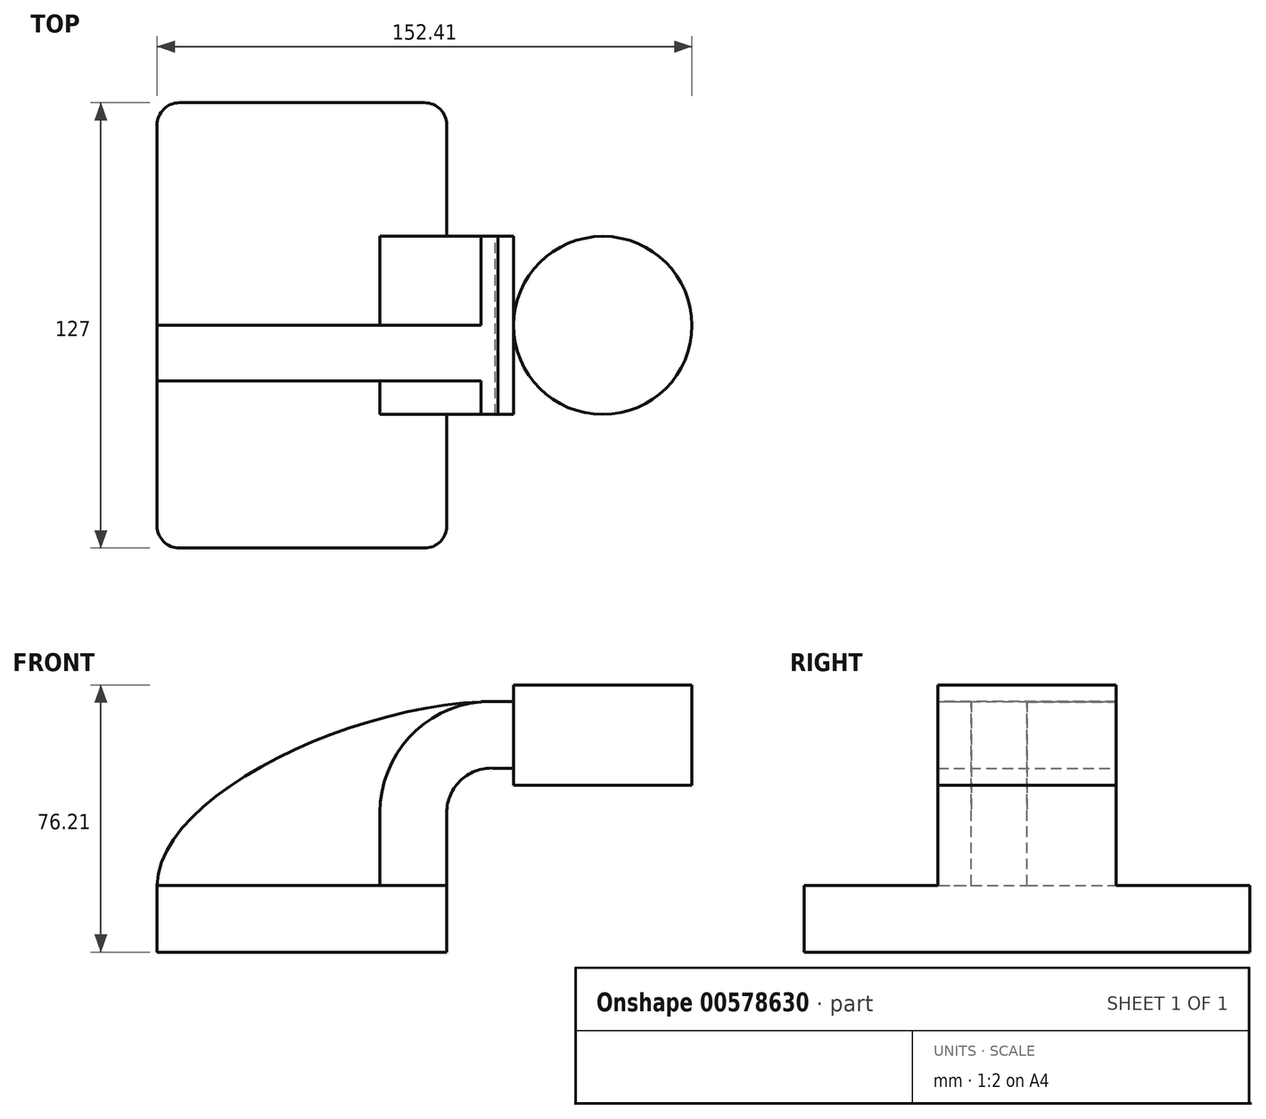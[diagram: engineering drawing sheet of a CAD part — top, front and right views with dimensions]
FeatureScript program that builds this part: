
annotation { "Feature Type Name" : "Feature", "Feature Type Description" : "" }
export const myFeature = defineFeature(function(context is Context, id is Id, definition is map)
    precondition{}
    {
        {
            var Q0;
            Q0=qCreatedBy(makeId("Front.planeOp"),FACE);
            var sketch = newSketch(context, id + "F0", { "sketchPlane" : qUnion([Q0])});
            skLineSegment(sketch, "E0.bottom", {"start": v(-41.28, 9.52) * mm, "end": v(41.27, 9.53) * mm});
            skLineSegment(sketch, "E0.top", {"start": v(-41.28, -9.53) * mm, "end": v(41.28, -9.53) * mm});
            skLineSegment(sketch, "E0.left", {"start": v(-41.28, 9.52) * mm, "end": v(-41.27, -9.53) * mm});
            skLineSegment(sketch, "E0.right", {"start": v(41.28, 9.53) * mm, "end": v(41.28, -9.52) * mm});
            skPoint(sketch, "E0.middle", {"position": v(0, 0) * mm});
            skLineSegment(sketch, "E1.bottom", {"start": v(60.32, 66.68) * mm, "end": v(111.12, 66.68) * mm});
            skLineSegment(sketch, "E1.top", {"start": v(60.33, 38.1) * mm, "end": v(111.13, 38.1) * mm});
            skLineSegment(sketch, "E1.left", {"start": v(60.32, 66.67) * mm, "end": v(60.33, 38.1) * mm});
            skLineSegment(sketch, "E1.right", {"start": v(111.12, 66.67) * mm, "end": v(111.13, 38.1) * mm});
            skPoint(sketch, "E1.middle", {"position": v(85.73, 52.39) * mm});
            skLineSegment(sketch, "E2", {"start": v(41.27, 9.53) * mm, "end": v(41.27, 30.28) * mm});
            skArc(sketch, "E3", {"start": v(41.28, 30.28) * mm, "mid": v(45.42, 39.64) * mm, "end": v(55.15, 42.88) * mm});
            skLineSegment(sketch, "E4", {"start": v(55.15, 42.88) * mm, "end": v(85.73, 42.88) * mm});
            skLineSegment(sketch, "E5", {"start": v(85.73, 42.88) * mm, "end": v(82.92, 42.88) * mm});
            skLineSegment(sketch, "E6.0", {"start": v(55.85, 61.93) * mm, "end": v(85.72, 61.93) * mm});
            skArc(sketch, "E6.1", {"start": v(22.23, 30.28) * mm, "mid": v(32.2, 53.37) * mm, "end": v(55.85, 61.93) * mm});
            skLineSegment(sketch, "E6.2", {"start": v(22.22, 9.53) * mm, "end": v(22.22, 30.28) * mm});
            skLineSegment(sketch, "E7", {"start": v(85.73, 38.1) * mm, "end": v(85.73, 66.67) * mm});
            skFitSpline(sketch, "E8", {"points": [v(-41.28, 9.53) * mm, v(55.85, 61.93) * mm], "startDerivative": vector(1.82, 79.2) * mm, "endDerivative": vector(116.48, -1.34) * mm});
            skSolve(sketch);
        }
        {
            var Q0;
            Q0=makeQuery(id+"F0.imprint","IMPRINT",FACE,{"disambiguationData":[TD([[makeQuery(id+"F0.imprint","IMPRINT",EDGE,{"derivedFrom":sQuery(id+"F0.wireOp",EDGE,"E0.top")}),1.0]])]});
            extrude(context, id + "F1", {"entities" : qUnion([Q0]), "endBound" : BoundingType.SYMMETRIC, "depth" : 127 * mm, "offsetDistance" : 25.4 * mm});
        }
        {
            var Q0;
            {var subQ1=sQuery(id+"F0.wireOp",EDGE,"E2");Q0=makeQuery(id+"F0.imprint","IMPRINT",FACE,{"disambiguationData":[TD([[makeQuery(id+"F0.imprint","IMPRINT",EDGE,{"derivedFrom":subQ1}),1.0]])]});}
            var Q1;
            {var subQ5=sQuery(id+"F0.wireOp",EDGE,"E5");Q1=makeQuery(id+"F0.imprint","IMPRINT",FACE,{"disambiguationData":[TD([[makeQuery(id+"F0.imprint","IMPRINT",EDGE,{"derivedFrom":subQ5}),-1.0]])]});}
            extrude(context, id + "F2", {"entities" : qUnion([Q0, Q1]), "operationType" : NewBodyOperationType.ADD, "endBound" : BoundingType.SYMMETRIC, "depth" : 50.8 * mm, "offsetDistance" : 25.4 * mm});
        }
        {
            var Q0;
            {var subQ3=sQuery(id+"F0.wireOp",EDGE,"E6.2");Q0=makeQuery(id+"F0.imprint","IMPRINT",FACE,{"disambiguationData":[TD([[makeQuery(id+"F0.imprint","IMPRINT",EDGE,{"derivedFrom":subQ3}),1.0]])]});}
            extrude(context, id + "F3", {"entities" : qUnion([Q0]), "operationType" : NewBodyOperationType.ADD, "depth" : 15.88 * mm, "offsetDistance" : 25.4 * mm});
        }
        {
            var Q0;
            {var subQ0=sQuery(id+"F0.wireOp",EDGE,"E1.right");Q0=makeQuery(id+"F0.imprint","IMPRINT",FACE,{"disambiguationData":[TD([[makeQuery(id+"F0.imprint","IMPRINT",EDGE,{"derivedFrom":subQ0}),-1.0]])]});}
            var Q1;
            Q1=sQuery(id+"F0.wireOp",EDGE,"E7");
            revolve(context, id + "F4", {"operationType" : NewBodyOperationType.ADD, "entities" : qUnion([Q0]), "axis" : qUnion([Q1]), "revolveType" : RevolveType.FULL});
        }
        {
            var Q0;
            Q0=makeQuery(id+"F1.opExtrude","CAP_EDGE",EDGE,{"disambiguationData":[OSD([sQuery(id+"F0.wireOp",EDGE,"E0.right")])],"isStart":false});
            var Q1;
            Q1=makeQuery(id+"F1.opExtrude","CAP_EDGE",EDGE,{"disambiguationData":[OSD([sQuery(id+"F0.wireOp",EDGE,"E0.right")])],"isStart":true});
            var Q2;
            Q2=makeQuery(id+"F1.opExtrude","CAP_EDGE",EDGE,{"disambiguationData":[OSD([sQuery(id+"F0.wireOp",EDGE,"E0.left")])],"isStart":false});
            var Q3;
            Q3=makeQuery(id+"F1.opExtrude","CAP_EDGE",EDGE,{"disambiguationData":[OSD([sQuery(id+"F0.wireOp",EDGE,"E0.left")])],"isStart":true});
            fillet(context, id + "F5", {"entities" : qUnion([Q0, Q1, Q2, Q3]), "radius" : 6.35 * mm, "tangentPropagation" : true, "allowEdgeOverflow" : false});
        }
    });
